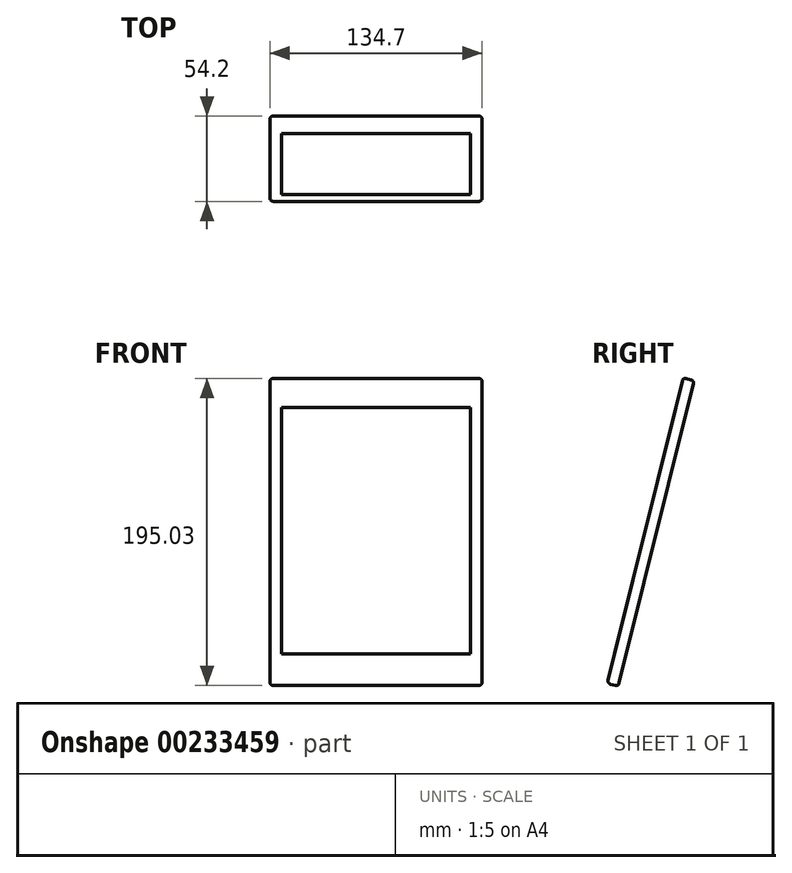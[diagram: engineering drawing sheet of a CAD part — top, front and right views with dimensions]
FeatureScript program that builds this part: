
annotation { "Feature Type Name" : "Feature", "Feature Type Description" : "" }
export const myFeature = defineFeature(function(context is Context, id is Id, definition is map)
    precondition{}
    {
        {
            var Q0;
            Q0=qCreatedBy(makeId("Right.planeOp"),FACE);
            var sketch = newSketch(context, id + "F0", { "sketchPlane" : qUnion([Q0])});
            skLineSegment(sketch, "E0", {"start": v(0.48, 1.94) * mm, "end": v(48.54, 196.08) * mm});
            skLineSegment(sketch, "E1", {"start": v(41.55, 197.81) * mm, "end": v(-6.5, 3.67) * mm});
            skPoint(sketch, "E2.visualSharp", {"position": v(0, 0) * mm});
            skLineSegment(sketch, "E3", {"start": v(0.48, 1.94) * mm, "end": v(-6.5, 3.67) * mm});
            skLineSegment(sketch, "E4", {"start": v(48.54, 196.08) * mm, "end": v(41.55, 197.81) * mm});
            skSolve(sketch);
        }
        {
            var Q0;
            Q0=makeQuery(id+"F0.imprint","IMPRINT",FACE,{"disambiguationData":[TD([[makeQuery(id+"F0.imprint","IMPRINT",EDGE,{"derivedFrom":sQuery(id+"F0.wireOp",EDGE,"E0")}),1.0]])]});
            extrude(context, id + "F1", {"entities" : qUnion([Q0]), "depth" : 134.7 * mm});
        }
        {
            var Q0;
            Q0=makeQuery(id+"F1.opExtrude","SWEPT_FACE",FACE,{"disambiguationData":[OSD([sQuery(id+"F0.wireOp",EDGE,"E1")])]});
            var sketch = newSketch(context, id + "F2", { "sketchPlane" : qUnion([Q0])});
            skLineSegment(sketch, "E5", {"start": v(67.35, 202) * mm, "end": v(67.35, 182.7) * mm, "construction": true});
            skLineSegment(sketch, "E6", {"start": v(67.35, 2) * mm, "end": v(67.35, 21.3) * mm, "construction": true});
            skLineSegment(sketch, "E7", {"start": v(134.7, 102) * mm, "end": v(127.4, 102) * mm, "construction": true});
            skPoint(sketch, "E7.endSnap0", {"position": v(134.7, 102) * mm});
            skLineSegment(sketch, "E8", {"start": v(0, 102) * mm, "end": v(7.3, 102) * mm, "construction": true});
            skLineSegment(sketch, "E9", {"start": v(7.3, 102) * mm, "end": v(7.3, 182.7) * mm});
            skLineSegment(sketch, "E10", {"start": v(7.3, 182.7) * mm, "end": v(67.35, 182.7) * mm});
            skLineSegment(sketch, "E11", {"start": v(67.35, 182.7) * mm, "end": v(127.4, 182.7) * mm});
            skLineSegment(sketch, "E12", {"start": v(127.4, 182.7) * mm, "end": v(127.4, 102) * mm});
            skLineSegment(sketch, "E13", {"start": v(127.4, 21.3) * mm, "end": v(127.4, 102) * mm});
            skLineSegment(sketch, "E14", {"start": v(127.4, 21.3) * mm, "end": v(67.35, 21.3) * mm});
            skLineSegment(sketch, "E15", {"start": v(67.35, 21.3) * mm, "end": v(7.3, 21.3) * mm});
            skLineSegment(sketch, "E16", {"start": v(7.3, 21.3) * mm, "end": v(7.3, 102) * mm});
            skSolve(sketch);
        }
        {
            var Q0;
            Q0=makeQuery(id+"F1.opExtrude","CAP_EDGE",EDGE,{"disambiguationData":[OSD([sQuery(id+"F0.wireOp",EDGE,"E1")])],"isStart":true});
            var Q1;
            Q1=makeQuery(id+"F1.opExtrude","CAP_EDGE",EDGE,{"disambiguationData":[OSD([sQuery(id+"F0.wireOp",EDGE,"E0")])],"isStart":true});
            var Q2;
            Q2=makeQuery(id+"F1.opExtrude","SWEPT_EDGE",EDGE,{"disambiguationData":[OSD([sQuery(id+"F0.wireOp",EDGE,"E1"),sQuery(id+"F0.wireOp",EDGE,"E4")])]});
            var Q3;
            Q3=makeQuery(id+"F1.opExtrude","CAP_EDGE",EDGE,{"disambiguationData":[OSD([sQuery(id+"F0.wireOp",EDGE,"E4")])],"isStart":true});
            var Q4;
            Q4=makeQuery(id+"F1.opExtrude","SWEPT_EDGE",EDGE,{"disambiguationData":[OSD([sQuery(id+"F0.wireOp",EDGE,"E0"),sQuery(id+"F0.wireOp",EDGE,"E4")])]});
            var Q5;
            Q5=makeQuery(id+"F1.opExtrude","CAP_EDGE",EDGE,{"disambiguationData":[OSD([sQuery(id+"F0.wireOp",EDGE,"E4")])],"isStart":false});
            var Q6;
            Q6=makeQuery(id+"F1.opExtrude","CAP_EDGE",EDGE,{"disambiguationData":[OSD([sQuery(id+"F0.wireOp",EDGE,"E0")])],"isStart":false});
            var Q7;
            Q7=makeQuery(id+"F1.opExtrude","CAP_EDGE",EDGE,{"disambiguationData":[OSD([sQuery(id+"F0.wireOp",EDGE,"E1")])],"isStart":false});
            var Q8;
            Q8=makeQuery(id+"F1.opExtrude","CAP_EDGE",EDGE,{"disambiguationData":[OSD([sQuery(id+"F0.wireOp",EDGE,"E3")])],"isStart":false});
            var Q9;
            Q9=makeQuery(id+"F1.opExtrude","SWEPT_EDGE",EDGE,{"disambiguationData":[OSD([sQuery(id+"F0.wireOp",EDGE,"E1"),sQuery(id+"F0.wireOp",EDGE,"E3")])]});
            var Q10;
            Q10=makeQuery(id+"F1.opExtrude","SWEPT_EDGE",EDGE,{"disambiguationData":[OSD([sQuery(id+"F0.wireOp",EDGE,"E0"),sQuery(id+"F0.wireOp",EDGE,"E3")])]});
            var Q11;
            Q11=makeQuery(id+"F1.opExtrude","CAP_EDGE",EDGE,{"disambiguationData":[OSD([sQuery(id+"F0.wireOp",EDGE,"E3")])],"isStart":true});
            fillet(context, id + "F3", {"entities" : qUnion([Q0, Q1, Q2, Q3, Q4, Q5, Q6, Q7, Q8, Q9, Q10, Q11]), "radius" : 2 * mm, "tangentPropagation" : true, "allowEdgeOverflow" : false});
        }
        {
            var Q0;
            Q0=makeQuery(id+"F2.imprint","IMPRINT",FACE,{"disambiguationData":[TD([[makeQuery(id+"F2.imprint","IMPRINT",EDGE,{"derivedFrom":sQuery(id+"F2.wireOp",EDGE,"E9")}),-1.0]])]});
            extrude(context, id + "F4", {"entities" : qUnion([Q0]), "depth" : 0.01 * mm});
        }
    });
